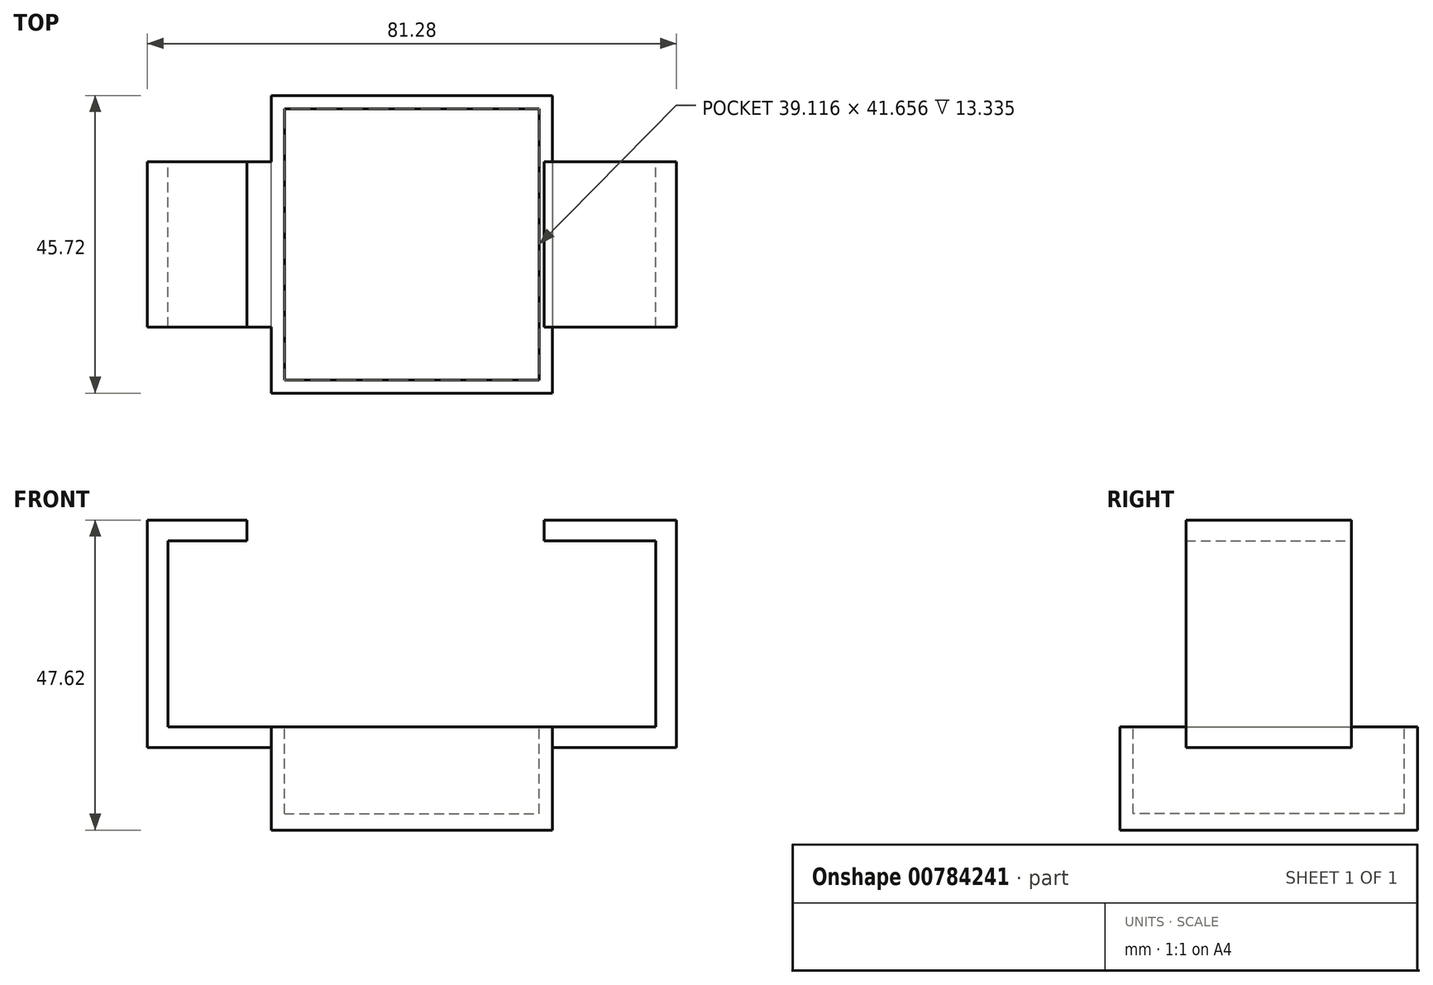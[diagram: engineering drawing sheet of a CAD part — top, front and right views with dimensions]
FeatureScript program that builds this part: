
annotation { "Feature Type Name" : "Feature", "Feature Type Description" : "" }
export const myFeature = defineFeature(function(context is Context, id is Id, definition is map)
    precondition{}
    {
        {
            var Q0;
            Q0=qCreatedBy(makeId("Front.planeOp"),FACE);
            var sketch = newSketch(context, id + "F0", { "sketchPlane" : qUnion([Q0])});
            skLineSegment(sketch, "E0", {"start": v(0, 0) * mm, "end": v(0, 34.92) * mm});
            skLineSegment(sketch, "E1", {"start": v(0, 34.92) * mm, "end": v(15.32, 34.92) * mm});
            skLineSegment(sketch, "E2", {"start": v(15.32, 34.92) * mm, "end": v(15.32, 31.75) * mm});
            skLineSegment(sketch, "E3", {"start": v(15.32, 31.75) * mm, "end": v(3.17, 31.75) * mm});
            skLineSegment(sketch, "E4", {"start": v(3.17, 31.75) * mm, "end": v(3.18, 3.17) * mm});
            skLineSegment(sketch, "E5", {"start": v(3.18, 3.17) * mm, "end": v(78.1, 3.18) * mm});
            skLineSegment(sketch, "E6", {"start": v(78.1, 3.18) * mm, "end": v(78.1, 31.75) * mm});
            skLineSegment(sketch, "E7", {"start": v(78.1, 31.75) * mm, "end": v(60.98, 31.75) * mm});
            skLineSegment(sketch, "E8", {"start": v(60.98, 31.75) * mm, "end": v(60.98, 34.93) * mm});
            skLineSegment(sketch, "E9", {"start": v(60.98, 34.93) * mm, "end": v(81.28, 34.93) * mm});
            skLineSegment(sketch, "E10", {"start": v(81.28, 34.93) * mm, "end": v(81.28, 0) * mm});
            skLineSegment(sketch, "E11", {"start": v(81.28, 0) * mm, "end": v(0, 0) * mm});
            skSolve(sketch);
        }
        {
            var Q0;
            Q0 = qSketchRegion(id + "F0", true);
            extrude(context, id + "F1", {"entities" : qUnion([Q0]), "depth" : 25.4 * mm, "offsetDistance" : 25.4 * mm});
        }
        {
            var Q0;
            Q0=makeQuery(id+"F1.opExtrude","SWEPT_FACE",FACE,{"disambiguationData":[OSD([sQuery(id+"F0.wireOp",EDGE,"E11")])]});
            var sketch = newSketch(context, id + "F2", { "sketchPlane" : qUnion([Q0])});
            skLineSegment(sketch, "E12", {"start": v(19.05, 35.56) * mm, "end": v(19.05, -10.16) * mm});
            skLineSegment(sketch, "E13", {"start": v(19.05, -10.16) * mm, "end": v(62.23, -10.16) * mm});
            skLineSegment(sketch, "E14", {"start": v(62.23, -10.16) * mm, "end": v(62.23, 35.56) * mm});
            skLineSegment(sketch, "E15", {"start": v(62.23, 35.56) * mm, "end": v(19.05, 35.56) * mm});
            skLineSegment(sketch, "E16.bottom", {"start": v(21.08, -8.13) * mm, "end": v(60.2, -8.13) * mm});
            skLineSegment(sketch, "E16.top", {"start": v(21.08, 33.53) * mm, "end": v(60.2, 33.53) * mm});
            skLineSegment(sketch, "E16.left", {"start": v(21.08, -8.13) * mm, "end": v(21.08, 33.53) * mm});
            skLineSegment(sketch, "E16.right", {"start": v(60.2, -8.13) * mm, "end": v(60.2, 33.53) * mm});
            skSolve(sketch);
        }
        {
            var Q0;
            Q0 = qSketchRegion(id + "F2", true);
            extrude(context, id + "F3", {"entities" : qUnion([Q0]), "operationType" : NewBodyOperationType.ADD, "depth" : 10.16 * mm, "offsetDistance" : 25.4 * mm});
        }
        {
            var Q0;
            Q0=makeQuery(id+"F3.opExtrude","CAP_FACE",FACE,{"disambiguationData":[OSD([sQuery(id+"F2.wireOp",EDGE,"E12"),sQuery(id+"F2.wireOp",EDGE,"E13"),sQuery(id+"F2.wireOp",EDGE,"E14"),sQuery(id+"F2.wireOp",EDGE,"E15"),sQuery(id+"F2.wireOp",EDGE,"E16.bottom"),sQuery(id+"F2.wireOp",EDGE,"E16.top"),sQuery(id+"F2.wireOp",EDGE,"E16.left"),sQuery(id+"F2.wireOp",EDGE,"E16.right")])],"isStart":false});
            var sketch = newSketch(context, id + "F4", { "sketchPlane" : qUnion([Q0])});
            skLineSegment(sketch, "E17.bottom", {"start": v(62.23, -10.16) * mm, "end": v(19.05, -10.16) * mm});
            skLineSegment(sketch, "E17.top", {"start": v(62.23, 35.56) * mm, "end": v(19.05, 35.56) * mm});
            skLineSegment(sketch, "E17.left", {"start": v(62.23, -10.16) * mm, "end": v(62.23, 35.56) * mm});
            skLineSegment(sketch, "E17.right", {"start": v(19.05, -10.16) * mm, "end": v(19.05, 35.56) * mm});
            skSolve(sketch);
        }
        {
            var Q0;
            Q0 = qSketchRegion(id + "F4", true);
            extrude(context, id + "F5", {"entities" : qUnion([Q0]), "operationType" : NewBodyOperationType.ADD, "depth" : 2.54 * mm, "offsetDistance" : 25.4 * mm});
        }
        {
            var Q0;
            Q0=makeQuery(id+"F1.opExtrude","CAP_FACE",FACE,{"disambiguationData":[OSD([sQuery(id+"F0.wireOp",EDGE,"E0"),sQuery(id+"F0.wireOp",EDGE,"E1"),sQuery(id+"F0.wireOp",EDGE,"E2"),sQuery(id+"F0.wireOp",EDGE,"E3"),sQuery(id+"F0.wireOp",EDGE,"E4"),sQuery(id+"F0.wireOp",EDGE,"E5"),sQuery(id+"F0.wireOp",EDGE,"E6"),sQuery(id+"F0.wireOp",EDGE,"E7"),sQuery(id+"F0.wireOp",EDGE,"E8"),sQuery(id+"F0.wireOp",EDGE,"E9"),sQuery(id+"F0.wireOp",EDGE,"E10"),sQuery(id+"F0.wireOp",EDGE,"E11")])],"isStart":true});
            var sketch = newSketch(context, id + "F6", { "sketchPlane" : qUnion([Q0])});
            skLineSegment(sketch, "E18", {"start": v(-60.2, 0) * mm, "end": v(-60.2, 3.18) * mm});
            skLineSegment(sketch, "E19", {"start": v(-60.2, 3.18) * mm, "end": v(-21.08, 3.17) * mm});
            skLineSegment(sketch, "E20", {"start": v(-21.08, 3.17) * mm, "end": v(-21.08, 0) * mm});
            skLineSegment(sketch, "E21", {"start": v(-21.08, 0) * mm, "end": v(-60.2, 0) * mm});
            skSolve(sketch);
        }
        {
            var Q0;
            Q0 = qSketchRegion(id + "F6", true);
            extrude(context, id + "F7", {"entities" : qUnion([Q0]), "operationType" : NewBodyOperationType.REMOVE, "oppositeDirection" : true, "depth" : 25.4 * mm, "offsetDistance" : 25.4 * mm});
        }
        {
            var Q0;
            {var subQ0=sQuery(id+"F2.wireOp",EDGE,"E12");var subQ2=sQuery(id+"F2.wireOp",EDGE,"E13");var subQ3=sQuery(id+"F2.wireOp",EDGE,"E14");var subQ4=sQuery(id+"F2.wireOp",EDGE,"E16.bottom");var subQ5=sQuery(id+"F2.wireOp",EDGE,"E16.left");var subQ6=sQuery(id+"F2.wireOp",EDGE,"E16.right");Q0=makeQuery(id+"F3.boolean.opBoolean","SPLIT",FACE,{"disambiguationData":[TD([makeQuery(id+"F3.opExtrude","SWEPT_FACE",FACE,{"disambiguationData":[OSD([subQ2])]})])],"derivedFrom":makeQuery(id+"F3.opExtrude","CAP_FACE",FACE,{"disambiguationData":[OSD([subQ0,subQ2,subQ3,sQuery(id+"F2.wireOp",EDGE,"E15"),subQ4,sQuery(id+"F2.wireOp",EDGE,"E16.top"),subQ5,subQ6])],"isStart":true})});}
            var sketch = newSketch(context, id + "F8", { "sketchPlane" : qUnion([Q0])});
            skLineSegment(sketch, "E22", {"start": v(19.05, 0) * mm, "end": v(21.08, 0) * mm});
            skLineSegment(sketch, "E23", {"start": v(21.08, 0) * mm, "end": v(21.08, 8.13) * mm});
            skLineSegment(sketch, "E24", {"start": v(21.08, 8.13) * mm, "end": v(60.2, 8.13) * mm});
            skLineSegment(sketch, "E25", {"start": v(60.2, 8.13) * mm, "end": v(60.2, 0) * mm});
            skLineSegment(sketch, "E26", {"start": v(60.2, 0) * mm, "end": v(62.23, 0) * mm});
            skLineSegment(sketch, "E27", {"start": v(62.23, 0) * mm, "end": v(62.23, 10.16) * mm});
            skLineSegment(sketch, "E28", {"start": v(62.23, 10.16) * mm, "end": v(19.05, 10.16) * mm});
            skLineSegment(sketch, "E29", {"start": v(19.05, 10.16) * mm, "end": v(19.05, 0) * mm});
            skSolve(sketch);
        }
        {
            var Q0;
            Q0 = qSketchRegion(id + "F8", true);
            extrude(context, id + "F9", {"entities" : qUnion([Q0]), "operationType" : NewBodyOperationType.ADD, "depth" : 3.17 * mm, "offsetDistance" : 25.4 * mm});
        }
        {
            var Q0;
            {var subQ0=sQuery(id+"F2.wireOp",EDGE,"E12");var subQ2=sQuery(id+"F2.wireOp",EDGE,"E14");var subQ3=sQuery(id+"F2.wireOp",EDGE,"E15");var subQ4=sQuery(id+"F2.wireOp",EDGE,"E16.top");var subQ5=sQuery(id+"F2.wireOp",EDGE,"E16.left");var subQ6=sQuery(id+"F2.wireOp",EDGE,"E16.right");Q0=makeQuery(id+"F3.boolean.opBoolean","SPLIT",FACE,{"disambiguationData":[TD([makeQuery(id+"F3.opExtrude","SWEPT_FACE",FACE,{"disambiguationData":[OSD([subQ3])]})])],"derivedFrom":makeQuery(id+"F3.opExtrude","CAP_FACE",FACE,{"disambiguationData":[OSD([subQ0,sQuery(id+"F2.wireOp",EDGE,"E13"),subQ2,subQ3,sQuery(id+"F2.wireOp",EDGE,"E16.bottom"),subQ4,subQ5,subQ6])],"isStart":true})});}
            var sketch = newSketch(context, id + "F10", { "sketchPlane" : qUnion([Q0])});
            skLineSegment(sketch, "E30", {"start": v(19.05, -25.4) * mm, "end": v(21.08, -25.4) * mm});
            skLineSegment(sketch, "E31", {"start": v(21.08, -25.4) * mm, "end": v(21.08, -33.53) * mm});
            skLineSegment(sketch, "E32", {"start": v(21.08, -33.53) * mm, "end": v(60.2, -33.53) * mm});
            skLineSegment(sketch, "E33", {"start": v(60.2, -33.53) * mm, "end": v(60.2, -25.4) * mm});
            skLineSegment(sketch, "E34", {"start": v(62.23, -35.56) * mm, "end": v(19.05, -35.56) * mm});
            skLineSegment(sketch, "E35", {"start": v(19.05, -35.56) * mm, "end": v(19.05, -25.4) * mm});
            skLineSegment(sketch, "E36", {"start": v(60.2, -25.4) * mm, "end": v(62.23, -25.4) * mm});
            skLineSegment(sketch, "E37", {"start": v(62.23, -25.4) * mm, "end": v(62.23, -35.56) * mm});
            skSolve(sketch);
        }
        {
            var Q0;
            Q0 = qSketchRegion(id + "F10", true);
            extrude(context, id + "F11", {"entities" : qUnion([Q0]), "operationType" : NewBodyOperationType.ADD, "depth" : 3.17 * mm, "offsetDistance" : 25.4 * mm});
        }
    });
